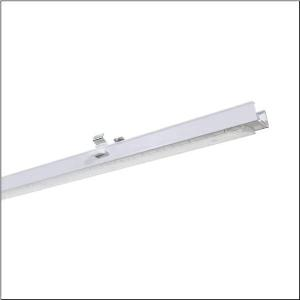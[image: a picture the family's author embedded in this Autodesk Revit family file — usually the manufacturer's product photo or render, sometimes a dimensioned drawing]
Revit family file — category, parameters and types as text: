
# Revit family: trunking_flex_31_51re14ma66b
name_source: partatom
category: Lighting Fixtures
units: mm (PartAtom-declared; Revit-internal decimal feet)

## family parameters
Cut with Voids When Loaded = No
Host = Face
Light Source = No
Part Type = Normal
Room Calculation Point = No
Round Connector Dimension = Use Diameter
Shared = No

## types (1)
- --- (1 x LED, 6400 lm, 40 W, 6500K)
    Apparent Load = 40 VA
    CIE Flux Codes = 72 92 98 99 100
    Color Rendering = 80
    Color Temperature = 6500K
    Default Elevation = 1800 mm
    Description = Trunking Flex 31, luminaire insert, of extruded aluminium section, coated, traffic white (RAL 9016), length: 1.172mm, width: 91mm, height: 53mm, LED rated luminous flux: 6.400lm, light colour: 865, control gear: ON/OFF Multilumen, with system connector: socket, mains connection: 220..240V, AC, 50/60Hz, rated input power: 40W, luminous flux adjustable on luminaire in four steps (3420/4540/5580/6630lm), connected load according to luminous flux setting (20/26/33/40W), primary light control with lens, of plastic, primary optical cover: cover, of PMMA, light emission: direct distribution, primary light characteristic: asymmetric, protection rating (complete): IP20, insulation class (complete): insulation class I (protective earthing), certification: CE, UKCA, impact resistance: IK02, permissible ambient temperature for indoor applications: -20..+40°C, packaging unit: 1 piece
    Height = 58 mm
    Lamp = 1 x LED
    Lamp Light Flux = 6400 lm
    Lamp Power = 40 W
    Lamp count = 1
    Length = 1172 mm
    Luminous efficacy = 160 lm/W
    Manufacturer = Siteco
    ModVariant = No
    Model = 51RE14MA66B
    Mounting Place = Ceiling
    Mounting Type = Pendant
    Number of Poles = 1
    OnlyDefault = Yes
    Power Factor = 1
    Product Name = Trunking Flex 31
    Product group = luminaire insert
    ProductGroupID = 901
    Protection Class = Protection class I
    Protection Degree = IP 20
    RLX_Detail_Level = 1
    RLX_Emergency_Light_Flux = 0 lm
    RLX_Emergency_Type = 0
    RLX_Emergency_Type_DB = No
    RlxData = <blob elided: 20725 chars, md5=6637ce44>
    Socket = socket
    Standby Power = 0 W
    System Light Flux = 6400 lm
    System Power = 40 W
    Type Comments = factory setting: luminous flux: 100 % | (ON | ON) | 300 mA
    Type Image = l_1266702.jpg
    URL = http://relux.com
    VarID = @adj_018767
    Voltage = 0 V
    Weight = 0.00 kg
    Width = 65 mm

## geometry (parser evidence)
native form markers: Blend x4, Sweep x10
no freeform markers — native parametric forms only
